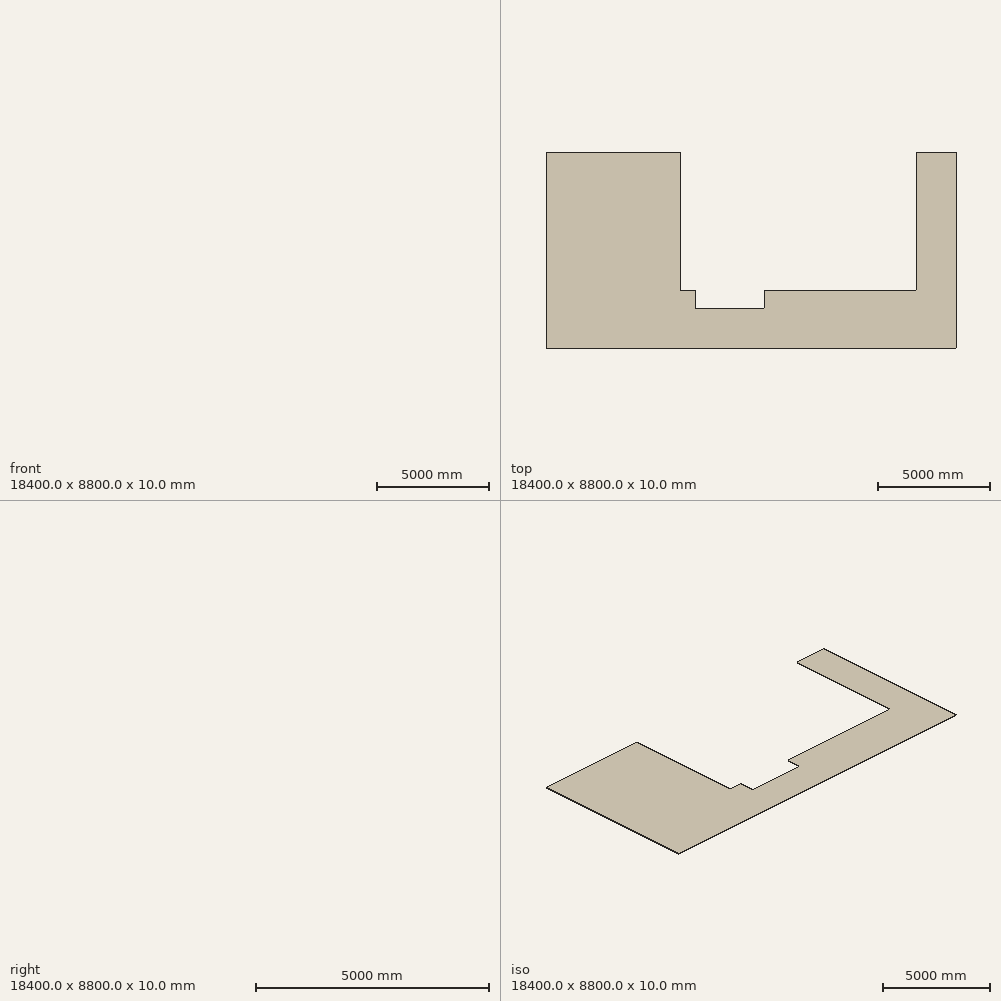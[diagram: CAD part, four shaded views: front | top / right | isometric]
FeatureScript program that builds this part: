
annotation { "Feature Type Name" : "Feature", "Feature Type Description" : "" }
export const myFeature = defineFeature(function(context is Context, id is Id, definition is map)
    precondition{}
    {
        {
            var Q0;
            Q0=qCreatedBy(makeId("Top.planeOp"),FACE);
            var sketch = newSketch(context, id + "F0", { "sketchPlane" : qUnion([Q0])});
            skLineSegment(sketch, "E0.top", {"start": v(-6000, -8800) * mm, "end": v(12400, -8800) * mm});
            skLineSegment(sketch, "E0.left", {"start": v(-6000, -3500) * mm, "end": v(-6000, -8800) * mm});
            skLineSegment(sketch, "E0.right", {"start": v(12400, 0) * mm, "end": v(12400, -8800) * mm});
            skLineSegment(sketch, "E1.top", {"start": v(0, -6200) * mm, "end": v(700, -6200) * mm});
            skLineSegment(sketch, "E1.left", {"start": v(0, 0) * mm, "end": v(0, -6200) * mm});
            skLineSegment(sketch, "E2.top", {"start": v(3800, -7000) * mm, "end": v(700, -7000) * mm});
            skLineSegment(sketch, "E2.left", {"start": v(3800, -6200) * mm, "end": v(3800, -7000) * mm});
            skLineSegment(sketch, "E2.right", {"start": v(700, -6200) * mm, "end": v(700, -7000) * mm});
            skLineSegment(sketch, "E3.trimOffspring", {"start": v(3800, -6200) * mm, "end": v(10600, -6200) * mm});
            skLineSegment(sketch, "E4.bottom", {"start": v(-6000, 0) * mm, "end": v(0, 0) * mm});
            skLineSegment(sketch, "E4.right", {"start": v(10600, 0) * mm, "end": v(10600, -6200) * mm});
            skLineSegment(sketch, "E5.trimOffspring", {"start": v(10600, 0) * mm, "end": v(12400, 0) * mm});
            skLineSegment(sketch, "E6.top", {"start": v(-6000, -3500) * mm, "end": v(-6000, -3500) * mm});
            skLineSegment(sketch, "E6.right", {"start": v(-6000, 0) * mm, "end": v(-6000, -3500) * mm});
            skSolve(sketch);
        }
        {
            var Q0;
            Q0 = qSketchRegion(id + "F0", true);
            extrude(context, id + "F1", {"entities" : qUnion([Q0]), "depth" : 10 * mm});
        }
    });
